# Revit family: Leather_Desks_BIM
name_source: partatom
category: Arredi
units: mm (PartAtom-declared; Revit-internal decimal feet)

## family parameters
Attiva taglio nelle viste = No
Basato su piano di lavoro = No
Condiviso = No
Numero OmniClass = 23.40.20.00
Origine composizione di rendering = Geometria famiglia
Punto di calcolo locali = No
Sempre verticale = Sì
Taglio con vuoti quando caricato = No
Titolo OmniClass = General Furniture and Specialties

## types (3) — shared parameters
AVAILABLE FINISHES = Hand rubbed natural oil on Walnut (NA), or hand rubbed black oil on Walnut (BO).
BASE MATERIAL = BASSAM_FELLOWS_OAK_O-NA
BIM BADGE = https://bim.archiproducts.com
COLLECTION = Leather Desk
HEIGHT = 720 mm  [stored 2.3622 ft]
MATERIAL DESCRIPTION = Carved, solid wood. Leather inset top and drawer linings.
PRODUCT SHEET = https://www.archiproducts.com
Produttore = BassamFellows
TECHNICAL SHEET = https://bassamfellows.com
UPHOLSTERY MATERIAL = BASSAM_FELLOWS_COMFORT_LEATHER_43632_CAMEL
URL = https://bassamfellows.com
zero-valued in all types: Prospetto di default

## per-type parameters (varying)
| type | DEPTH | Descrizione | Modello | WIDTH |
| CB-311P | 750 mm  [stored 2.46063 ft] | Solid wood desk with leather top | Leather Desk Petit | 1200 mm |
| CB-311 | 850 mm  [stored 2.78871 ft] | Solid wood desk with leather top | Leather Desk | 1820 mm |
| CB-311-90 | 900 mm  [stored 2.95276 ft] | Solid wood games table with leather top | Leather Games Table | 900 mm  [stored 2.95276 ft] |

note: column(s) folded — value = type name in every type: PRODUCT CODE

note: [stored X ft] marks values corroborated as IEEE doubles in the binary element streams (Revit-internal decimal feet)

## geometry (parser evidence)
native form markers: Sweep x3
no freeform markers — native parametric forms only
